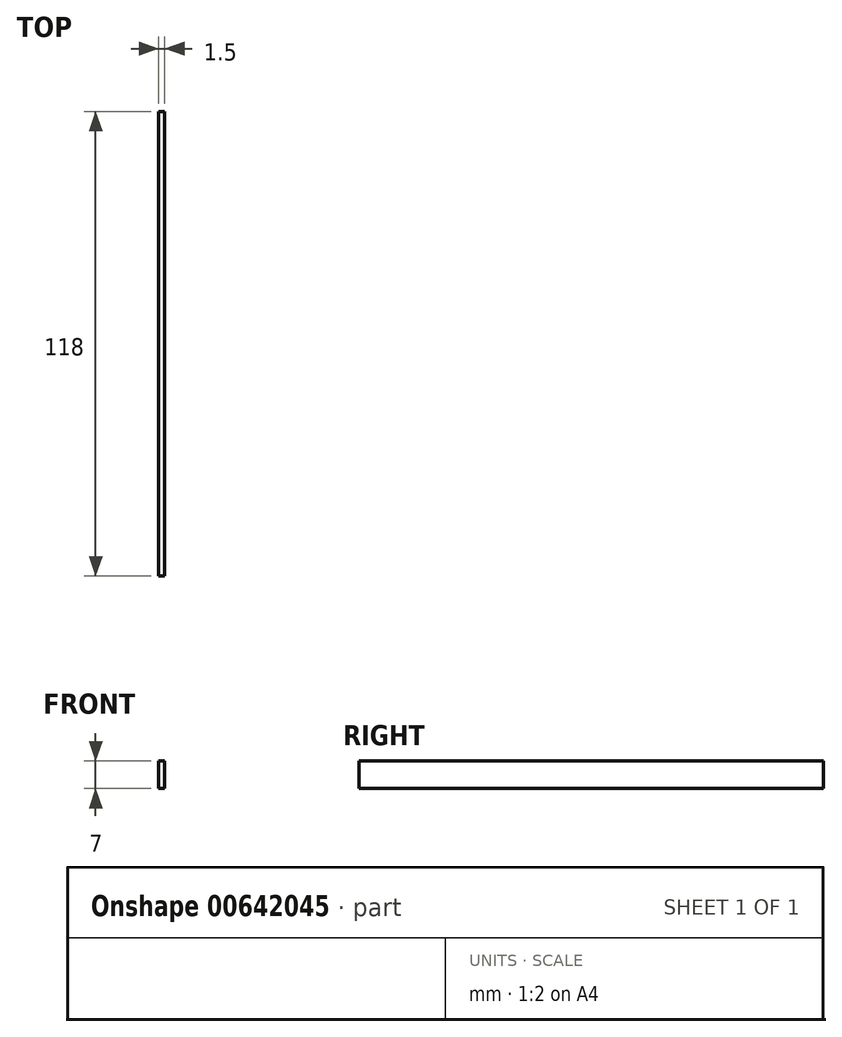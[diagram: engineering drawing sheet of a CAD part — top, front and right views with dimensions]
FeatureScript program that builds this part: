
annotation { "Feature Type Name" : "Feature", "Feature Type Description" : "" }
export const myFeature = defineFeature(function(context is Context, id is Id, definition is map)
    precondition{}
    {
        {
            var Q0;
            Q0=qCreatedBy(makeId("Right.planeOp"),FACE);
            var sketch = newSketch(context, id + "F0", { "sketchPlane" : qUnion([Q0])});
            skLineSegment(sketch, "E0.bottom", {"start": v(-66.84, 13.05) * mm, "end": v(51.16, 13.05) * mm});
            skLineSegment(sketch, "E0.top", {"start": v(-66.84, 6.05) * mm, "end": v(51.16, 6.05) * mm});
            skLineSegment(sketch, "E0.left", {"start": v(-66.84, 13.05) * mm, "end": v(-66.84, 6.05) * mm});
            skLineSegment(sketch, "E0.right", {"start": v(51.16, 13.05) * mm, "end": v(51.16, 6.05) * mm});
            skSolve(sketch);
        }
        {
            var Q0;
            Q0=makeQuery(id+"F0.imprint","IMPRINT",FACE,{"disambiguationData":[TD([[makeQuery(id+"F0.imprint","IMPRINT",EDGE,{"derivedFrom":sQuery(id+"F0.wireOp",EDGE,"E0.bottom")}),-1.0]])]});
            extrude(context, id + "F1", {"entities" : qUnion([Q0]), "depth" : 1.5 * mm, "offsetDistance" : 25 * mm});
        }
    });
